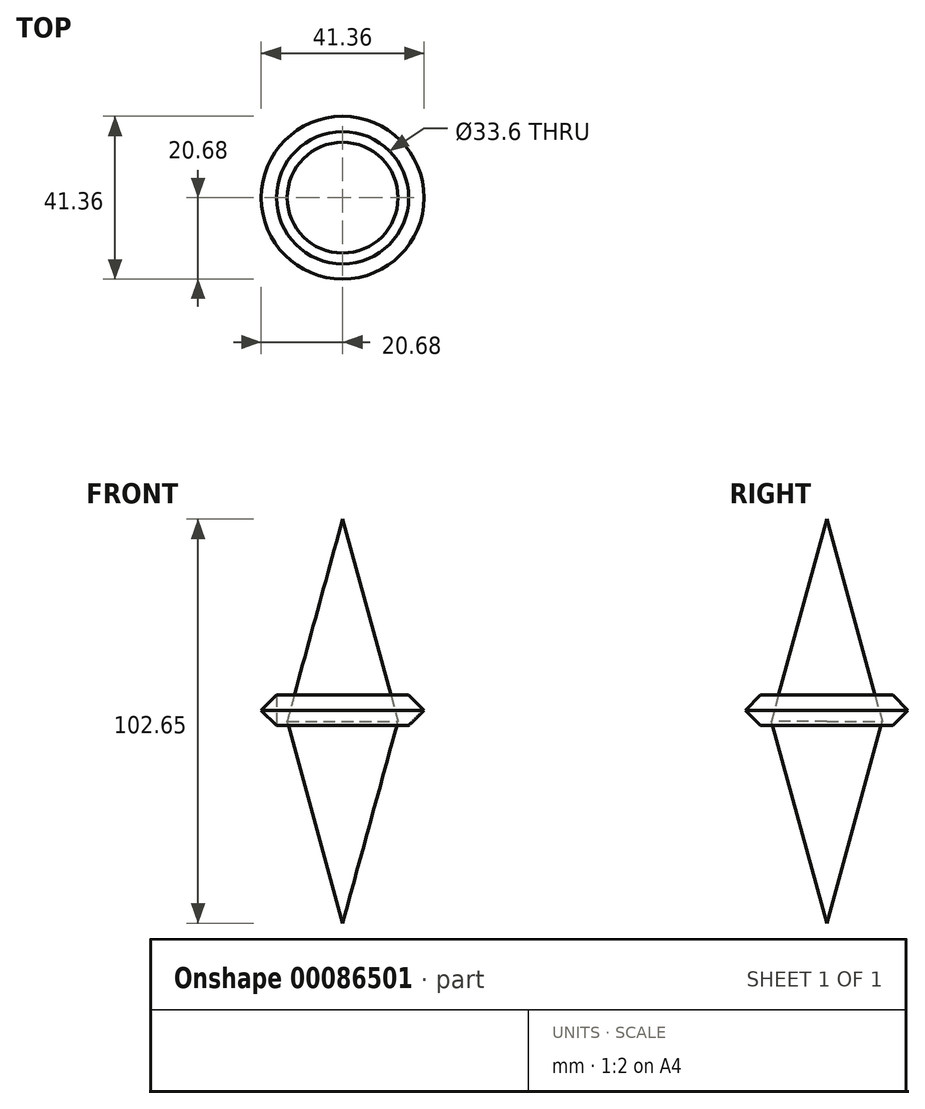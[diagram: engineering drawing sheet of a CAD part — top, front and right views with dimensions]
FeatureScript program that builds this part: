
annotation { "Feature Type Name" : "Feature", "Feature Type Description" : "" }
export const myFeature = defineFeature(function(context is Context, id is Id, definition is map)
    precondition{}
    {
        {
            var Q0;
            Q0=qCreatedBy(makeId("Front.planeOp"),FACE);
            var sketch = newSketch(context, id + "F0", { "sketchPlane" : qUnion([Q0])});
            skLineSegment(sketch, "E0", {"start": v(0, 48.54) * mm, "end": v(-14.08, -2.79) * mm});
            skLineSegment(sketch, "E1", {"start": v(-14.08, -2.79) * mm, "end": v(0, -54.11) * mm});
            skLineSegment(sketch, "E2", {"start": v(0, -54.11) * mm, "end": v(0, 48.54) * mm});
            skSolve(sketch);
        }
        {
            var Q0;
            Q0 = qSketchRegion(id + "F0", true);
            var Q1;
            Q1=sQuery(id+"F0.wireOp",EDGE,"E2");
            revolve(context, id + "F1", {"entities" : qUnion([Q0]), "axis" : qUnion([Q1]), "revolveType" : RevolveType.FULL});
        }
        {
            var Q0;
            Q0=qCreatedBy(makeId("Top.planeOp"),FACE);
            var sketch = newSketch(context, id + "F2", { "sketchPlane" : qUnion([Q0])});
            skCircle(sketch, "E3", {"center": v(0, 0) * mm, "radius": 16.8 * mm});
            skCircle(sketch, "E4", {"center": v(0, 0) * mm, "radius": 20.68 * mm});
            skSolve(sketch);
        }
        {
            var Q0;
            Q0 = qSketchRegion(id + "F2", true);
            extrude(context, id + "F3", {"entities" : qUnion([Q0]), "endBound" : BoundingType.SYMMETRIC, "depth" : 10 * mm});
        }
        {
            var Q0;
            Q0=makeQuery(id+"F3.opExtrude","CAP_EDGE",EDGE,{"disambiguationData":[OSD([sQuery(id+"F2.wireOp",EDGE,"E4")])],"isStart":false});
            var Q1;
            Q1=makeQuery(id+"F3.opExtrude","CAP_EDGE",EDGE,{"disambiguationData":[OSD([sQuery(id+"F2.wireOp",EDGE,"E4")])],"isStart":true});
            chamfer(context, id + "F4", {"entities" : qUnion([Q0, Q1]), "width" : 5 * mm, "tangentPropagation" : true});
        }
    });
